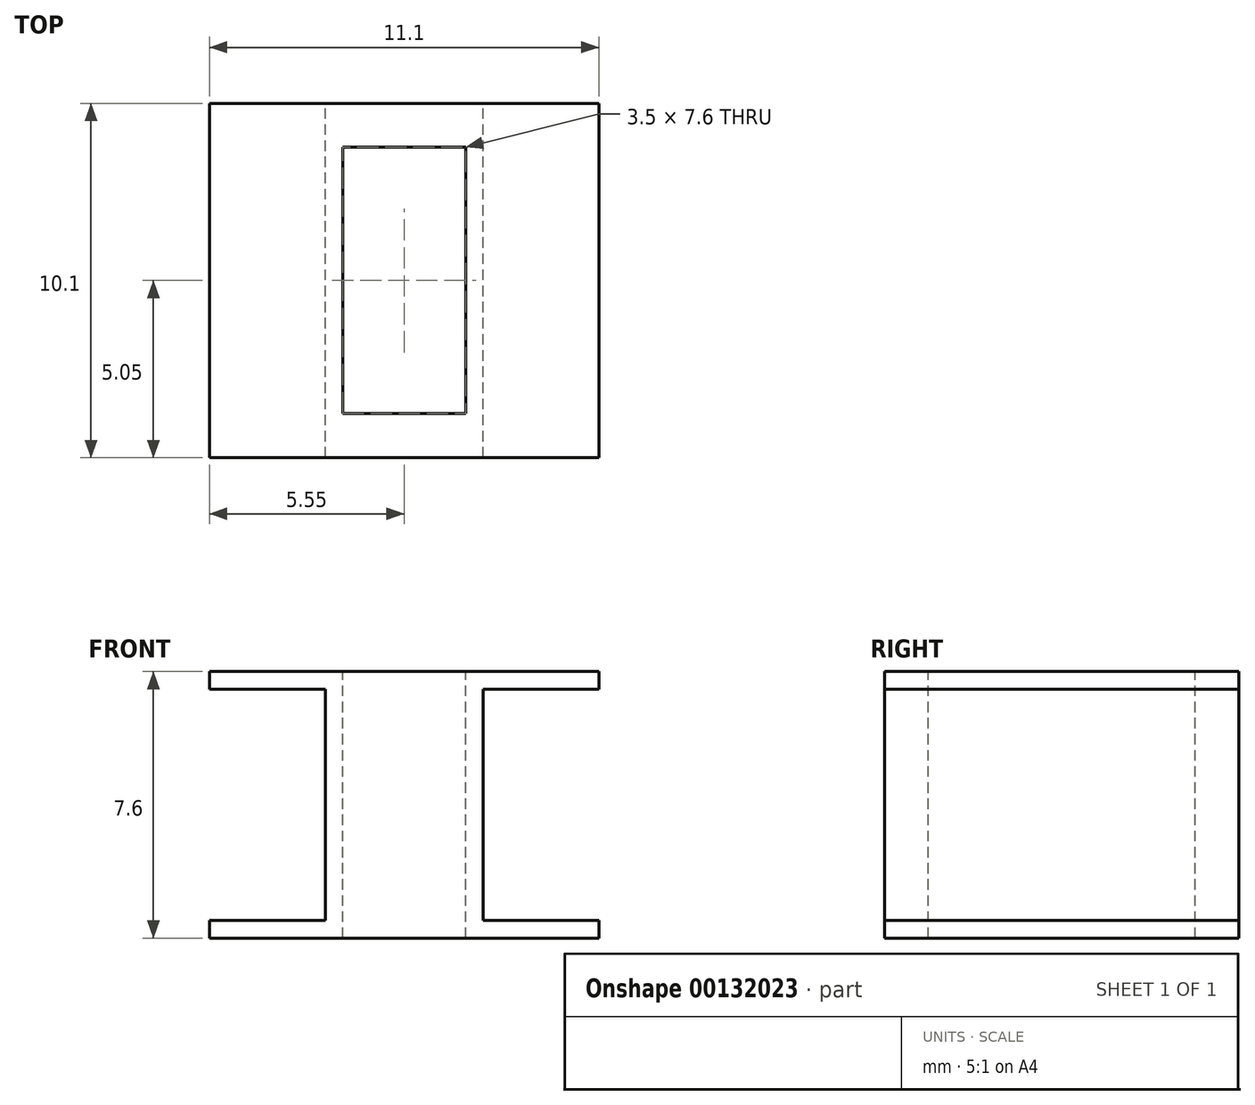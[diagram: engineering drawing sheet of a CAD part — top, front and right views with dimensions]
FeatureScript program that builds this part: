
annotation { "Feature Type Name" : "Feature", "Feature Type Description" : "" }
export const myFeature = defineFeature(function(context is Context, id is Id, definition is map)
    precondition{}
    {
        {
            var Q0;
            Q0=qCreatedBy(makeId("Front.planeOp"),FACE);
            var sketch = newSketch(context, id + "F0", { "sketchPlane" : qUnion([Q0])});
            skLineSegment(sketch, "E0.left", {"start": v(-0.8, 3.3) * mm, "end": v(-0.8, -3.3) * mm});
            skLineSegment(sketch, "E0.right", {"start": v(3.7, 3.3) * mm, "end": v(3.7, -3.3) * mm});
            skLineSegment(sketch, "E1.bottom", {"start": v(-4.1, 3.8) * mm, "end": v(7, 3.8) * mm});
            skLineSegment(sketch, "E1.top", {"start": v(-4.1, -3.8) * mm, "end": v(7, -3.8) * mm});
            skLineSegment(sketch, "E2", {"start": v(-0.8, 3.3) * mm, "end": v(-4.1, 3.3) * mm});
            skLineSegment(sketch, "E3", {"start": v(-4.1, 3.8) * mm, "end": v(-4.1, 3.3) * mm});
            skLineSegment(sketch, "E4", {"start": v(3.7, 3.3) * mm, "end": v(7, 3.3) * mm});
            skLineSegment(sketch, "E5", {"start": v(7, 3.8) * mm, "end": v(7, 3.3) * mm});
            skLineSegment(sketch, "E6", {"start": v(-0.8, -3.3) * mm, "end": v(-4.1, -3.3) * mm});
            skLineSegment(sketch, "E7", {"start": v(-4.1, -3.3) * mm, "end": v(-4.1, -3.8) * mm});
            skLineSegment(sketch, "E8", {"start": v(3.7, -3.3) * mm, "end": v(7, -3.3) * mm});
            skLineSegment(sketch, "E9", {"start": v(7, -3.3) * mm, "end": v(7, -3.8) * mm});
            skSolve(sketch);
        }
        {
            var Q0;
            Q0=makeQuery(id+"F0.imprint","IMPRINT",FACE,{"disambiguationData":[TD([[makeQuery(id+"F0.imprint","IMPRINT",EDGE,{"derivedFrom":sQuery(id+"F0.wireOp",EDGE,"E0.left")}),1.0]])]});
            extrude(context, id + "F1", {"entities" : qUnion([Q0]), "depth" : 10.1 * mm});
        }
        {
            var Q0;
            Q0=makeQuery(id+"F1.opExtrude","SWEPT_FACE",FACE,{"disambiguationData":[OSD([sQuery(id+"F0.wireOp",EDGE,"E1.bottom")])]});
            var sketch = newSketch(context, id + "F2", { "sketchPlane" : qUnion([Q0])});
            skLineSegment(sketch, "E10.bottom", {"start": v(-0.3, -1.25) * mm, "end": v(3.2, -1.25) * mm});
            skLineSegment(sketch, "E10.top", {"start": v(-0.3, -8.85) * mm, "end": v(3.2, -8.85) * mm});
            skLineSegment(sketch, "E10.left", {"start": v(-0.3, -1.25) * mm, "end": v(-0.3, -8.85) * mm});
            skLineSegment(sketch, "E10.right", {"start": v(3.2, -1.25) * mm, "end": v(3.2, -8.85) * mm});
            skSolve(sketch);
        }
        {
            var Q0;
            Q0=makeQuery(id+"F2.imprint","IMPRINT",FACE,{"disambiguationData":[TD([[makeQuery(id+"F2.imprint","IMPRINT",EDGE,{"derivedFrom":sQuery(id+"F2.wireOp",EDGE,"E10.bottom")}),-1.0]])]});
            extrude(context, id + "F3", {"entities" : qUnion([Q0]), "operationType" : NewBodyOperationType.REMOVE, "oppositeDirection" : true, "depth" : 10 * mm});
        }
    });
